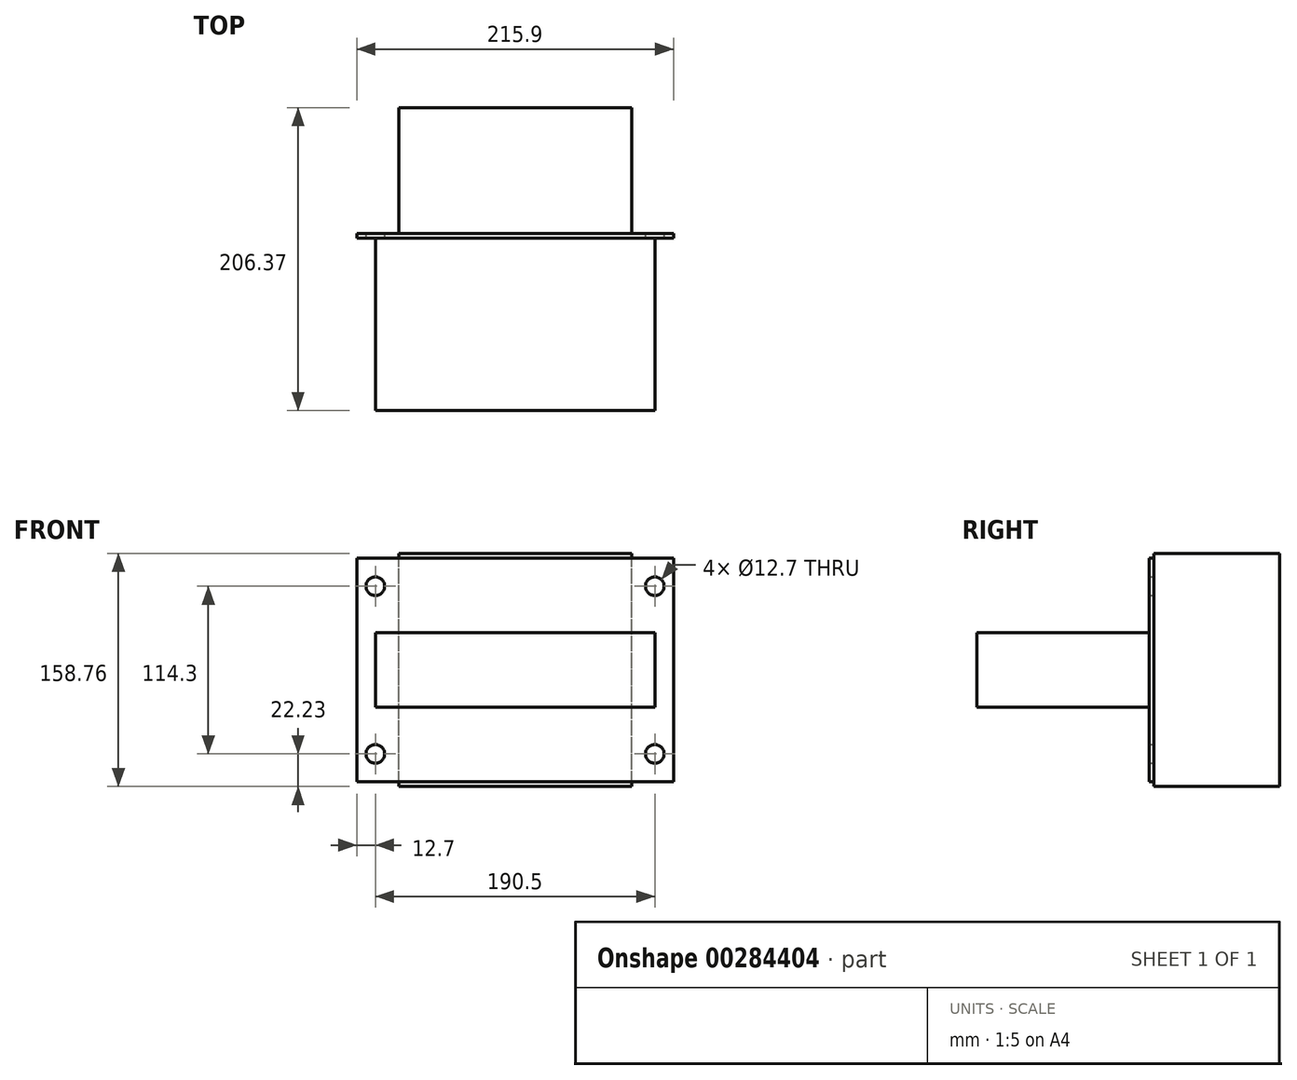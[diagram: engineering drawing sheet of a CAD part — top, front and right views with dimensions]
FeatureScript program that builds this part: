
annotation { "Feature Type Name" : "Feature", "Feature Type Description" : "" }
export const myFeature = defineFeature(function(context is Context, id is Id, definition is map)
    precondition{}
    {
        {
            var Q0;
            Q0=qCreatedBy(makeId("Front.planeOp"),FACE);
            var sketch = newSketch(context, id + "F0", { "sketchPlane" : qUnion([Q0])});
            skLineSegment(sketch, "E0", {"start": v(107.95, 0) * mm, "end": v(-107.95, 0) * mm, "construction": true});
            skLineSegment(sketch, "E1.bottom", {"start": v(95.25, -25.4) * mm, "end": v(-95.25, -25.4) * mm});
            skLineSegment(sketch, "E1.top", {"start": v(95.25, 25.4) * mm, "end": v(-95.25, 25.4) * mm});
            skLineSegment(sketch, "E1.left", {"start": v(95.25, -25.4) * mm, "end": v(95.25, 25.4) * mm});
            skLineSegment(sketch, "E1.right", {"start": v(-95.25, -25.4) * mm, "end": v(-95.25, 25.4) * mm});
            skPoint(sketch, "E1.middle", {"position": v(0, 0) * mm});
            skCircle(sketch, "E2", {"center": v(-95.25, 57.15) * mm, "radius": 6.35 * mm});
            skCircle(sketch, "E3.0.1.0", {"center": v(-95.25, -57.15) * mm, "radius": 6.35 * mm});
            skCircle(sketch, "E3.1.0.0", {"center": v(95.25, 57.15) * mm, "radius": 6.35 * mm});
            skCircle(sketch, "E3.1.1.0", {"center": v(95.25, -57.15) * mm, "radius": 6.35 * mm});
            skLineSegment(sketch, "E3.direction1", {"start": v(-95.25, 57.15) * mm, "end": v(95.25, 57.15) * mm, "construction": true});
            skLineSegment(sketch, "E3.direction2", {"start": v(-95.25, 57.15) * mm, "end": v(-95.25, -57.15) * mm, "construction": true});
            skLineSegment(sketch, "E4.bottom", {"start": v(107.95, 76.2) * mm, "end": v(-107.95, 76.2) * mm});
            skLineSegment(sketch, "E4.top", {"start": v(107.95, -76.2) * mm, "end": v(-107.95, -76.2) * mm});
            skLineSegment(sketch, "E4.left", {"start": v(107.95, 76.2) * mm, "end": v(107.95, -76.2) * mm});
            skLineSegment(sketch, "E4.right", {"start": v(-107.95, 76.2) * mm, "end": v(-107.95, -76.2) * mm});
            skLineSegment(sketch, "E5.bottom", {"start": v(79.38, -79.37) * mm, "end": v(-79.37, -79.38) * mm});
            skLineSegment(sketch, "E5.top", {"start": v(79.38, 79.38) * mm, "end": v(-79.37, 79.37) * mm});
            skLineSegment(sketch, "E5.left", {"start": v(79.38, -79.38) * mm, "end": v(79.38, 79.38) * mm});
            skLineSegment(sketch, "E5.right", {"start": v(-79.37, -79.38) * mm, "end": v(-79.37, 79.38) * mm});
            skSolve(sketch);
        }
        {
            var Q0;
            {var subQ0=sQuery(id+"F0.wireOp",EDGE,"E5.left");var subQ1=sQuery(id+"F0.wireOp",EDGE,"E1.bottom");var subQ2=makeQuery(id+"F0.imprint","INTERSECT",VERTEX,{"derivedFrom":[subQ1,subQ0]});Q0=makeQuery(id+"F0.imprint","IMPRINT",FACE,{"disambiguationData":[TD([[makeQuery(id+"F0.imprint","IMPRINT",EDGE,{"disambiguationData":[TD([[subQ2,-1.0]])],"derivedFrom":subQ1}),1.0]])]});}
            var Q1;
            {var subQ0=sQuery(id+"F0.wireOp",EDGE,"E5.left");var subQ1=sQuery(id+"F0.wireOp",EDGE,"E1.top");var subQ2=makeQuery(id+"F0.imprint","INTERSECT",VERTEX,{"derivedFrom":[subQ1,subQ0]});Q1=makeQuery(id+"F0.imprint","IMPRINT",FACE,{"disambiguationData":[TD([[makeQuery(id+"F0.imprint","IMPRINT",EDGE,{"disambiguationData":[TD([[subQ2,-1.0]])],"derivedFrom":subQ1}),-1.0]])]});}
            var Q2;
            {var subQ0=sQuery(id+"F0.wireOp",EDGE,"E1.left");Q2=makeQuery(id+"F0.imprint","IMPRINT",FACE,{"disambiguationData":[TD([[makeQuery(id+"F0.imprint","IMPRINT",EDGE,{"derivedFrom":subQ0}),-1.0]])]});}
            var Q3;
            {var subQ6=sQuery(id+"F0.wireOp",EDGE,"E1.right");Q3=makeQuery(id+"F0.imprint","IMPRINT",FACE,{"disambiguationData":[TD([[makeQuery(id+"F0.imprint","IMPRINT",EDGE,{"derivedFrom":subQ6}),1.0]])]});}
            var Q4;
            {var subQ0=sQuery(id+"F0.wireOp",EDGE,"E5.left");var subQ1=sQuery(id+"F0.wireOp",EDGE,"E1.bottom");var subQ2=makeQuery(id+"F0.imprint","INTERSECT",VERTEX,{"derivedFrom":[subQ1,subQ0]});Q4=makeQuery(id+"F0.imprint","IMPRINT",FACE,{"disambiguationData":[TD([[makeQuery(id+"F0.imprint","IMPRINT",EDGE,{"disambiguationData":[TD([[subQ2,-1.0]])],"derivedFrom":subQ1}),-1.0]])]});}
            var Q5;
            {var subQ0=sQuery(id+"F0.wireOp",EDGE,"E1.right");Q5=makeQuery(id+"F0.imprint","IMPRINT",FACE,{"disambiguationData":[TD([[makeQuery(id+"F0.imprint","IMPRINT",EDGE,{"derivedFrom":subQ0}),-1.0]])]});}
            var Q6;
            {var subQ0=sQuery(id+"F0.wireOp",EDGE,"E1.left");Q6=makeQuery(id+"F0.imprint","IMPRINT",FACE,{"disambiguationData":[TD([[makeQuery(id+"F0.imprint","IMPRINT",EDGE,{"derivedFrom":subQ0}),1.0]])]});}
            extrude(context, id + "F1", {"entities" : qUnion([Q0, Q1, Q2, Q3, Q4, Q5, Q6]), "depth" : 3.17 * mm});
        }
        {
            var Q0;
            {var subQ0=sQuery(id+"F0.wireOp",EDGE,"E5.left");var subQ1=sQuery(id+"F0.wireOp",EDGE,"E1.bottom");var subQ2=makeQuery(id+"F0.imprint","INTERSECT",VERTEX,{"derivedFrom":[subQ1,subQ0]});Q0=makeQuery(id+"F0.imprint","IMPRINT",FACE,{"disambiguationData":[TD([[makeQuery(id+"F0.imprint","IMPRINT",EDGE,{"disambiguationData":[TD([[subQ2,-1.0]])],"derivedFrom":subQ1}),1.0]])]});}
            var Q1;
            {var subQ0=sQuery(id+"F0.wireOp",EDGE,"E5.left");var subQ1=sQuery(id+"F0.wireOp",EDGE,"E1.bottom");var subQ2=makeQuery(id+"F0.imprint","INTERSECT",VERTEX,{"derivedFrom":[subQ1,subQ0]});Q1=makeQuery(id+"F0.imprint","IMPRINT",FACE,{"disambiguationData":[TD([[makeQuery(id+"F0.imprint","IMPRINT",EDGE,{"disambiguationData":[TD([[subQ2,-1.0]])],"derivedFrom":subQ1}),-1.0]])]});}
            var Q2;
            {var subQ0=sQuery(id+"F0.wireOp",EDGE,"E5.left");var subQ1=sQuery(id+"F0.wireOp",EDGE,"E1.top");var subQ2=makeQuery(id+"F0.imprint","INTERSECT",VERTEX,{"derivedFrom":[subQ1,subQ0]});Q2=makeQuery(id+"F0.imprint","IMPRINT",FACE,{"disambiguationData":[TD([[makeQuery(id+"F0.imprint","IMPRINT",EDGE,{"disambiguationData":[TD([[subQ2,-1.0]])],"derivedFrom":subQ1}),-1.0]])]});}
            var Q3;
            {var subQ5=sQuery(id+"F0.wireOp",EDGE,"E5.top");Q3=makeQuery(id+"F0.imprint","IMPRINT",FACE,{"disambiguationData":[TD([[makeQuery(id+"F0.imprint","IMPRINT",EDGE,{"derivedFrom":subQ5}),1.0]])]});}
            var Q4;
            {var subQ5=sQuery(id+"F0.wireOp",EDGE,"E5.bottom");Q4=makeQuery(id+"F0.imprint","IMPRINT",FACE,{"disambiguationData":[TD([[makeQuery(id+"F0.imprint","IMPRINT",EDGE,{"derivedFrom":subQ5}),-1.0]])]});}
            extrude(context, id + "F2", {"entities" : qUnion([Q0, Q1, Q2, Q3, Q4]), "operationType" : NewBodyOperationType.ADD, "oppositeDirection" : true, "depth" : 85.72 * mm});
        }
        {
            var Q0;
            {var subQ0=sQuery(id+"F0.wireOp",EDGE,"E1.right");Q0=makeQuery(id+"F0.imprint","IMPRINT",FACE,{"disambiguationData":[TD([[makeQuery(id+"F0.imprint","IMPRINT",EDGE,{"derivedFrom":subQ0}),-1.0]])]});}
            var Q1;
            {var subQ0=sQuery(id+"F0.wireOp",EDGE,"E5.left");var subQ1=sQuery(id+"F0.wireOp",EDGE,"E1.bottom");var subQ2=makeQuery(id+"F0.imprint","INTERSECT",VERTEX,{"derivedFrom":[subQ1,subQ0]});Q1=makeQuery(id+"F0.imprint","IMPRINT",FACE,{"disambiguationData":[TD([[makeQuery(id+"F0.imprint","IMPRINT",EDGE,{"disambiguationData":[TD([[subQ2,-1.0]])],"derivedFrom":subQ1}),-1.0]])]});}
            var Q2;
            {var subQ0=sQuery(id+"F0.wireOp",EDGE,"E1.left");Q2=makeQuery(id+"F0.imprint","IMPRINT",FACE,{"disambiguationData":[TD([[makeQuery(id+"F0.imprint","IMPRINT",EDGE,{"derivedFrom":subQ0}),1.0]])]});}
            extrude(context, id + "F3", {"entities" : qUnion([Q0, Q1, Q2]), "operationType" : NewBodyOperationType.ADD, "depth" : 120.65 * mm});
        }
    });
